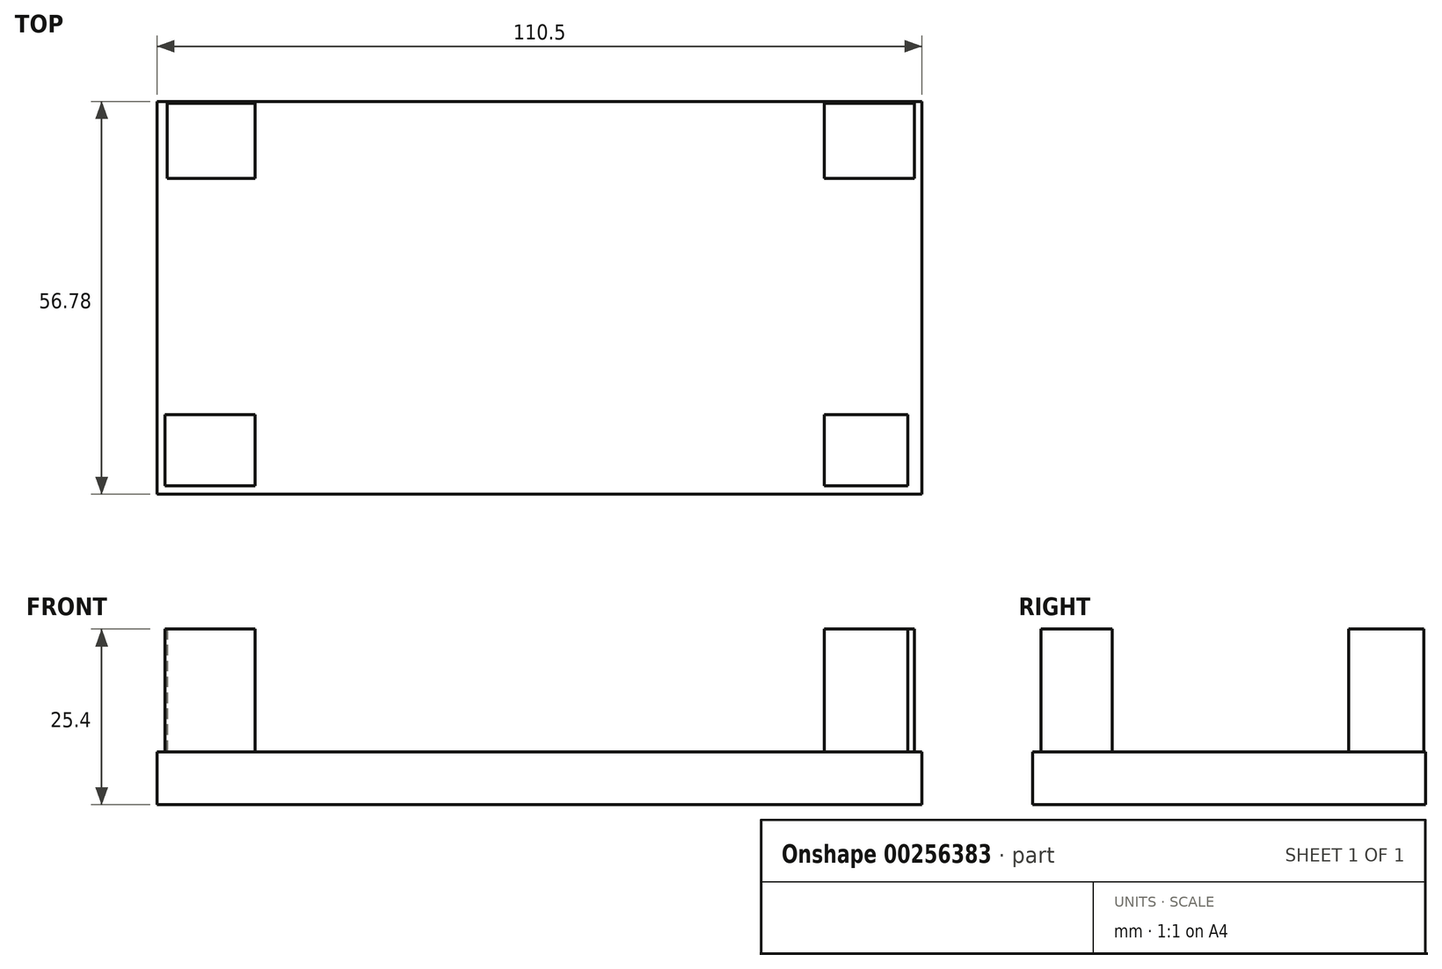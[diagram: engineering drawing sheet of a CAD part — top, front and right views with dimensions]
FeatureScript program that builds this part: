
annotation { "Feature Type Name" : "Feature", "Feature Type Description" : "" }
export const myFeature = defineFeature(function(context is Context, id is Id, definition is map)
    precondition{}
    {
        {
            var Q0;
            Q0=qCreatedBy(makeId("Top.planeOp"),FACE);
            var sketch = newSketch(context, id + "F0", { "sketchPlane" : qUnion([Q0])});
            skLineSegment(sketch, "E0.bottom", {"start": v(55.25, -28.39) * mm, "end": v(-55.25, -28.39) * mm});
            skLineSegment(sketch, "E0.top", {"start": v(55.25, 28.39) * mm, "end": v(-55.25, 28.39) * mm});
            skLineSegment(sketch, "E0.left", {"start": v(55.25, -28.39) * mm, "end": v(55.25, 28.39) * mm});
            skLineSegment(sketch, "E0.right", {"start": v(-55.25, -28.39) * mm, "end": v(-55.25, 28.39) * mm});
            skPoint(sketch, "E0.middle", {"position": v(0, 0) * mm});
            skSolve(sketch);
        }
        {
            var Q0;
            Q0=makeQuery(id+"F0.imprint","IMPRINT",FACE,{"disambiguationData":[TD([[makeQuery(id+"F0.imprint","IMPRINT",EDGE,{"derivedFrom":sQuery(id+"F0.wireOp",EDGE,"E0.bottom")}),-1.0]])]});
            var sketch = newSketch(context, id + "F1", { "sketchPlane" : qUnion([Q0])});
            skLineSegment(sketch, "E1.bottom", {"start": v(-53.82, 28.13) * mm, "end": v(-41.12, 28.13) * mm});
            skLineSegment(sketch, "E1.top", {"start": v(-53.82, 17.25) * mm, "end": v(-41.12, 17.25) * mm});
            skLineSegment(sketch, "E1.left", {"start": v(-53.82, 28.13) * mm, "end": v(-53.82, 17.25) * mm});
            skLineSegment(sketch, "E1.right", {"start": v(-41.12, 28.13) * mm, "end": v(-41.12, 17.25) * mm});
            skLineSegment(sketch, "E2.bottom", {"start": v(54.13, 28.13) * mm, "end": v(41.12, 28.13) * mm});
            skLineSegment(sketch, "E2.top", {"start": v(54.13, 17.25) * mm, "end": v(41.12, 17.25) * mm});
            skLineSegment(sketch, "E2.left", {"start": v(54.13, 28.13) * mm, "end": v(54.13, 17.25) * mm});
            skLineSegment(sketch, "E2.right", {"start": v(41.12, 28.13) * mm, "end": v(41.12, 17.25) * mm});
            skLineSegment(sketch, "E3.bottom", {"start": v(53.22, -27.2) * mm, "end": v(41.12, -27.2) * mm});
            skLineSegment(sketch, "E3.top", {"start": v(53.22, -16.92) * mm, "end": v(41.12, -16.92) * mm});
            skLineSegment(sketch, "E3.left", {"start": v(53.22, -27.2) * mm, "end": v(53.22, -16.92) * mm});
            skLineSegment(sketch, "E3.right", {"start": v(41.12, -27.2) * mm, "end": v(41.12, -16.92) * mm});
            skLineSegment(sketch, "E4.bottom", {"start": v(-54.13, -27.2) * mm, "end": v(-41.12, -27.2) * mm});
            skLineSegment(sketch, "E4.top", {"start": v(-54.13, -16.92) * mm, "end": v(-41.12, -16.92) * mm});
            skLineSegment(sketch, "E4.left", {"start": v(-54.13, -27.2) * mm, "end": v(-54.13, -16.92) * mm});
            skLineSegment(sketch, "E4.right", {"start": v(-41.12, -27.2) * mm, "end": v(-41.12, -16.92) * mm});
            skSolve(sketch);
        }
        {
            var Q0;
            Q0=qCreatedBy(makeId("Top.planeOp"),FACE);
            var sketch = newSketch(context, id + "F2", { "sketchPlane" : qUnion([Q0])});
            skSolve(sketch);
        }
        {
            var Q0;
            Q0 = qSketchRegion(id + "F2", true);
            var Q1;
            Q1=makeQuery(id+"F0.imprint","IMPRINT",FACE,{"disambiguationData":[TD([[makeQuery(id+"F0.imprint","IMPRINT",EDGE,{"derivedFrom":sQuery(id+"F0.wireOp",EDGE,"E0.bottom")}),-1.0]])]});
            extrude(context, id + "F3", {"entities" : qUnion([Q0, Q1]), "depth" : 7.62 * mm});
        }
        {
            var Q0;
            Q0=makeQuery(id+"F1.imprint","IMPRINT",FACE,{"disambiguationData":[TD([[makeQuery(id+"F1.imprint","IMPRINT",EDGE,{"derivedFrom":sQuery(id+"F1.wireOp",EDGE,"E2.bottom")}),1.0]])]});
            var Q1;
            Q1=makeQuery(id+"F1.imprint","IMPRINT",FACE,{"disambiguationData":[TD([[makeQuery(id+"F1.imprint","IMPRINT",EDGE,{"derivedFrom":sQuery(id+"F1.wireOp",EDGE,"E3.bottom")}),-1.0]])]});
            var Q2;
            Q2=makeQuery(id+"F1.imprint","IMPRINT",FACE,{"disambiguationData":[TD([[makeQuery(id+"F1.imprint","IMPRINT",EDGE,{"derivedFrom":sQuery(id+"F1.wireOp",EDGE,"E4.bottom")}),1.0]])]});
            var Q3;
            Q3=makeQuery(id+"F1.imprint","IMPRINT",FACE,{"disambiguationData":[TD([[makeQuery(id+"F1.imprint","IMPRINT",EDGE,{"derivedFrom":sQuery(id+"F1.wireOp",EDGE,"E1.bottom")}),-1.0]])]});
            extrude(context, id + "F4", {"entities" : qUnion([Q0, Q1, Q2, Q3]), "operationType" : NewBodyOperationType.ADD, "depth" : 25.4 * mm});
        }
    });
